# Revit family: Gleiter radial-axial GL-100 m.Lasche, 2xAG
name_source: partatom
category: HLS-Bauteile
revit_build: Autodesk Revit 2017 (Build: 20190507_1515(x64)
units: mm (PartAtom-declared; Revit-internal decimal feet)

## family parameters
Arbeitsebenenbasiert = Ja
Beim Laden mit Abzugskörper schneiden = Nein
Bemaßung runder Anschluss = Durchmesser verwenden
Gemeinsam genutzt = Ja
Immer vertikal = Nein
Raumberechnungspunkt = Nein
Teiletyp = Normal

## types (4) — shared parameters
B = 160 mm  [stored 0.524934 ft]
B1 = 50 mm  [stored 0.164042 ft]
Breite = 186 mm  [stored 0.610236 ft]
DVS = 14 mm  [stored 0.0459318 ft]
Fabrikat = MEFA
Gleitreibungsfaktor = 0.15 - 0.25
H1 = 7 mm  [stored 0.0229659 ft]
Haftreibungsfaktor = 0,2 - 0,3
Kurztext1 = Gleitelement radial-axial GL 100
L = 125 mm  [stored 0.410105 ft]
L1 = 96 mm  [stored 0.314961 ft]
Länge = 160 mm  [stored 0.524934 ft]
Material Gleitstreifen = Kunststoff
Materialname Gleitstreifen = Polyamid 6
Mengeneinheit = St
Vorgabe-Ansicht = 1219 mm
max. Temperaturbeständigkeit = 100 °C
vpe = 1 St

## per-type parameters (varying)
| type | Artikelnummer | EAN | Gewicht | Gewicht pro Bauteil | Gl-100, 2xAG | H | Kurztext2 |
| Gleiter ra-ax GL-100 m. Lasche, 2x M10 | 077048002 | 4250928417695 | 1.10 kg | 1.10 kg | Gleiter GL-100, 2xAG : Gleiter GL-100, 2x AG M10 | 47 mm  [stored 0.154199 ft] | Anschluss 2 x M10 mit Lasche |
| Gleiter ra-ax GL-100 m. Lasche, 2x M12 | 077048102 | 4250928417718 | 1.12 kg | 1.12 kg | Gleiter GL-100, 2xAG : Gleiter GL-100, 2x AG M12 | 49 mm  [stored 0.160761 ft] | Anschluss 2 x M12 mit Lasche |
| Gleiter ra-ax GL-100 m. Lasche, 2x M16 | 077048702 | 4250928417831 | 1.14 kg | 1.14 kg | Gleiter GL-100, 2xAG : Gleiter GL-100, 2x AG M16 | 48 mm  [stored 0.15748 ft] | Anschluss 2 x M16 mit Lasche |
| Gleiter ra-ax GL-100 m. Lasche, 2x 1/2" | 077048202 | 4250928417732 | 1.12 kg | 1.12 kg | Gleiter GL-100, 2xAG : Gleiter GL-100, 2x AG Muffe halbe Zoll | 48 mm  [stored 0.15748 ft] | Anschluss 2 x 1/2'' mit Lasche |

note: [stored X ft] marks values corroborated as IEEE doubles in the binary element streams (Revit-internal decimal feet)

## geometry (parser evidence)
native form markers: Sweep x4
no freeform markers — native parametric forms only
